# Revit family: MAGIC 1.3 LED LINEAR LIGHT
name_source: partatom
category: Lighting Fixtures
units: mm (PartAtom-declared; Revit-internal decimal feet)

## family parameters
Cut with Voids When Loaded = No
Host = Face
Light Source = Yes
Part Type = Normal
Room Calculation Point = No
Round Connector Dimension = Use Diameter
Shared = No

## types (18) — shared parameters
Apparent Load = 0 VA
Average life based on L70(HRS) = 100000
CRI = 90
Color Filter = 16777215
Default Elevation = 0' - 0"
Description = This MAGIC led linear fixture is a 1.3 wide, linear architectural luminaire with a slim and a discrete profile.
Dimming / Control = 0-10 V
Dimming Lamp Color Temperature Shift = <None>
Finish/Color = White Aluminum
Inside Element = white inside
Load Classification = Lighting
Manufacturer = Above All Lighting
Power Factor = 1
Tilt Angle = -90.00°
Type Comments = 1.3 MAGIC 1.3 LED LINEAR LIGHT
URL = https://www.abovealllighting.com
Voltage = 120-277 V

## per-type parameters (varying)
| type | B | Fixture Length | Photometric Web File | WATTS | Wattage Comments |
| MAG0613-SW1-PSM-SD-FDL | 0' - 7" | 2' - 0" | MAG0613_SW1_FDL_BLACK_DOWN100_4000K_.IES | 20 W | 20W/15W/10W |
| MAG0613-SW1-PSM-SD-DPL | 0' - 7" | 2' - 0" | MAG0613_SW1_DPL_BLACK_DOWN100_4000K_.IES | 20 W | 20W/15W/10W |
| MAG0613-SW1-PSM-SD-LVL | 0' - 7" | 2' - 0" | MAG0613_SW1_LVL_BLACK_UP25DOWN75_4000K_.IES | 20 W | 20W/15W/10W |
| MAG0613-351-PSM-SD-MRF | 0' - 7" | 2' - 0" | MAG06351-PM-A1-MRF.IES | 20 W | 20W/15W/10W |
| MAG0613-301-PSM-SD-MRF | 0' - 7" | 2' - 0" | generic.ies | 20 W | 20W/15W/10W |
| MAG0613-401-PSM-SD-MRF | 0' - 7" | 2' - 0" | generic.ies | 20 W | 20W/15W/10W |
| MAG1213-SW1-PSM-SD-FDL | 1' - 7" | 4' - 0" | MAG1223-FDL-WH (4000K, DOWN100%).IES | 40 W | 20W/15W/10W |
| MAG1213-SW1-PSM-SD-DPL | 1' - 7" | 4' - 0" | MAG1213_SW1_DPL_4000K_DOWN100_.IES | 20 W | 40W/30W/20W |
| MAG1213-SW1-PSM-SD-LVL | 1' - 7" | 4' - 0" | MAG1213_SW1_LVL_4000K_UP25DOWN75_.IES | 40 W | 40W/30W/20W |
| MAG1213-351-PSM-SD-MRF | 1' - 7" | 4' - 0" | MAG12351-PM-A1-MRF.IES | 40 W | 40W/30W/20W |
| MAG1213-301-PSM-SD-MRF | 1' - 7" | 4' - 0" | generic.ies | 40 W | 40W/30W/20W |
| MAG1213-401-PSM-SD-MRF | 1' - 7" | 4' - 0" | generic.ies | 40 W | 40W/30W/20W |
| MAG2413-SW1-PSM-SD-FDL | 3' - 7" | 8' - 0" | generic.ies | 80 W | 80W/60W/40W |
| MAG2413-SW1-PSM-SD-DPL | 3' - 7" | 8' - 0" | generic.ies | 80 W | 80W/60W/40W |
| MAG2413-SW1-PSM-SD-LVL | 3' - 7" | 8' - 0" | generic.ies | 80 W | 80W/60W/40W |
| MAG2413-351-PSM-SD-MRF | 3' - 7" | 8' - 0" | generic.ies | 80 W | 80W/60W/40W |
| MAG2413-301-PSM-SD-MRF | 3' - 7" | 8' - 0" | generic.ies | 80 W | 80W/60W/40W |
| MAG2413-401-PSM-SD-MRF | 3' - 7" | 8' - 0" | generic.ies | 80 W | 80W/60W/40W |

## geometry (parser evidence)
native form markers: Sweep x9
no freeform markers — native parametric forms only
